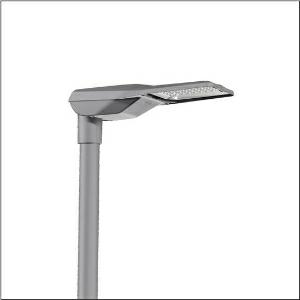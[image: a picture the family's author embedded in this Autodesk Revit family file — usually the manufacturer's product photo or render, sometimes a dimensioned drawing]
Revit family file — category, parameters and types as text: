
# Revit family: streetlight_sl_21_iq_mini___pl52_5xe2h41g08gb_5dc3
name_source: partatom
category: Lighting Fixtures
units: mm (PartAtom-declared; Revit-internal decimal feet)

## family parameters
Cut with Voids When Loaded = No
Host = Face
Light Source = No
Part Type = Normal
Room Calculation Point = No
Round Connector Dimension = Use Diameter
Shared = No

## types (1)
- --- (1 x LED, 5810 lm, 37.1 W, 4000K)
    Apparent Load = 37 VA
    CIE Flux Codes = 27 59 98 100 100
    Color Rendering = 70
    Color Temperature = 4000K
    Default Elevation = 1800 mm
    Description = Streetlight SL 21 iQ mini, mast luminaire, primary light control with lens, of PMMA, primary optical cover: cover, of toughened safety glass, transparent, light distribution: PL52, light emission: direct distribution, primary light characteristic: asymmetric, installation type: post-top, side-entry, LED, High Power LED, rated luminous flux: 5.810lm, luminous efficacy: 157lm/W, light colour: 740, colour temperature: 4000K, control gear: iQ Street-Remote, control: Street-Remote, Auto-Match, Temp-Guard, Lumen-Switch, Night-Set, Smart-Wire, Light-Fading, Desk-Remote (wireless, voltage-free reading and setting of iQ features in the workshop via application-optimized NFC function/RFID function), optimised constant luminous flux control (CLO 2.0), pre-setting: linear dimming characteristic, mains connection: 220..240V, AC, 50/60Hz, start of lifetime: 37W, end of service life: 39W, reduction: 18W, luminaire housing, of diecast aluminium, powder-coated, SITECO metallic grey (DB 702S), corrosivity category C5 high according to DIN EN ISO 12944, please order mast flange separately, inclination adjustable: 0°, 5°, 10°, 15°, sealing non-destructively replaceable, multi-level sealing system, length: 628mm, width: 235mm, height: 110mm, mast flange for spigot size: 42mm (side-entry): 5XC10008XM4, 60/48mm (side-entry/post-top): 5XC10108XM2, 76/60mm (side-entry/post-top): 5XC10108XM1, mounting height: 4..8m, protection rating (complete): IP66, insulation class (complete): insulation class II (safety insulation), certification: CE, ENEC, ENEC+, VDE, impact resistance: IK10, permissible operating ambient temperature for outdoor applications: -40..+50°C, standard-compliant lighting for roads and squares, packaging unit: 1 piece

Light Distribution: PL52
    Height = 110 mm
    Lamp = 1 x LED
    Lamp Light Flux = 5810 lm
    Lamp Power = 37.1 W
    Lamp count = 1
    Length = 625 mm
    Luminous efficacy = 157 lm/W
    Manufacturer = Siteco
    ModVariant = No
    Model = 5XE2H41G08GB
    Number of Poles = 1
    OnlyDefault = Yes
    Power Factor = 1
    Product Name = Streetlight SL 21 iQ mini | PL52
    Product group = mast luminaire | pylon top
    ProductGroupID = 6100
    Protection Class = Protection class II
    Protection Degree = IP 66
    RLX_Detail_Level = 1
    RLX_Emergency_Light_Flux = 0 lm
    RLX_Emergency_Type = 0
    RLX_Emergency_Type_DB = No
    RlxData = <blob elided: 36017 chars, md5=76465447>
    Socket = socket
    Standby Power = 0 W
    System Light Flux = 5810 lm
    System Power = 37 W
    Type Comments = factory setting: luminous flux: 100 % | dim-lin: 254 | 385 mA
    Type Image = l_1003519.jpg
    URL = http://relux.com
    VarID = @adj_187707
    Voltage = 0 V
    Weight = 0.00 kg
    Width = 234 mm

## geometry (parser evidence)
native form markers: Blend x4, Sweep x9
no freeform markers — native parametric forms only
